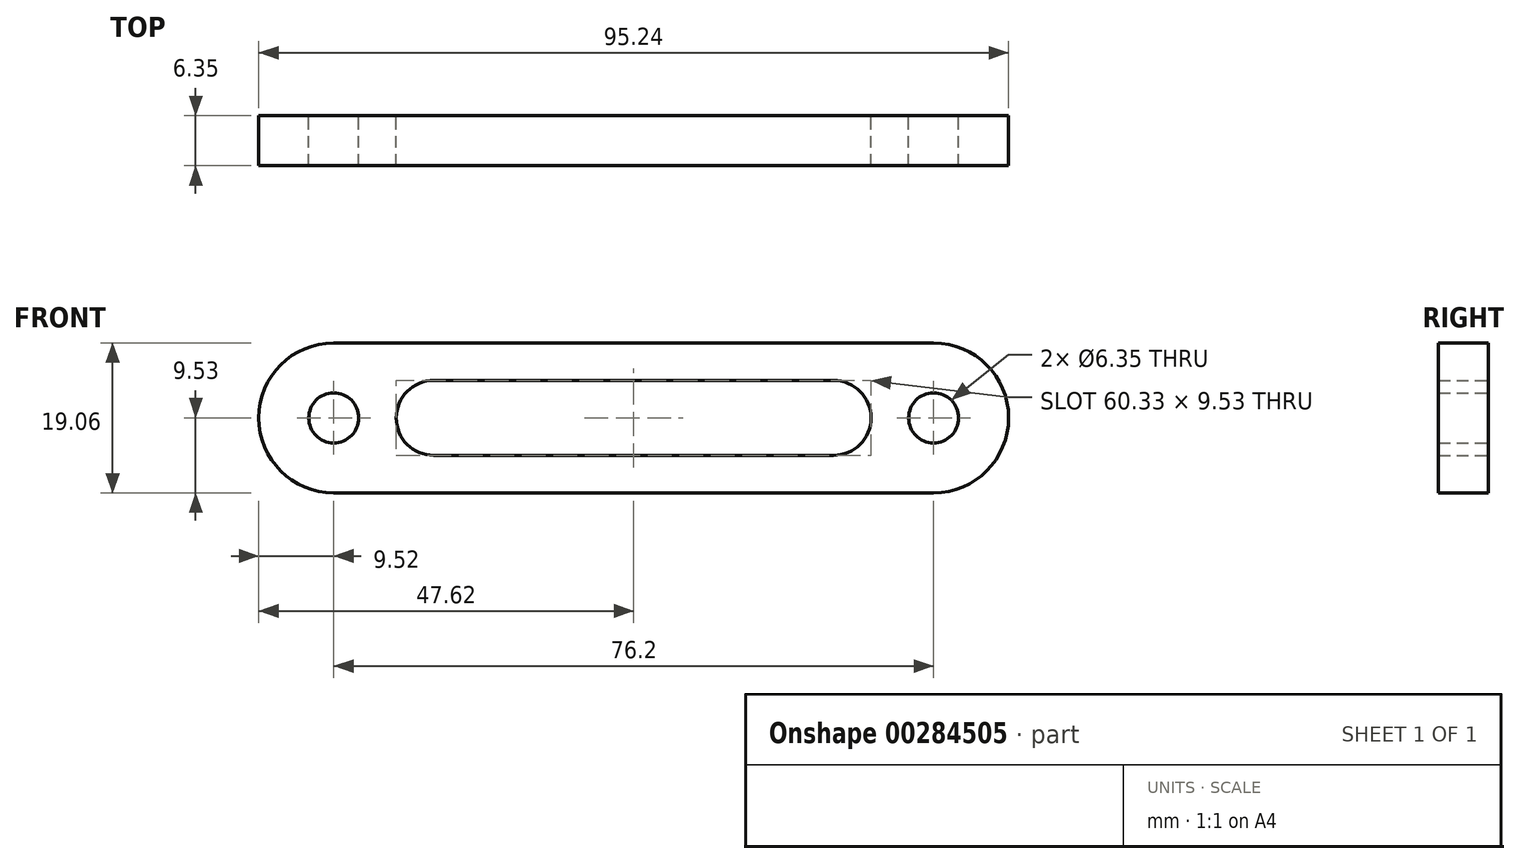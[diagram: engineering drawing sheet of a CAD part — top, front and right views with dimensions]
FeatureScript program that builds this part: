
annotation { "Feature Type Name" : "Feature", "Feature Type Description" : "" }
export const myFeature = defineFeature(function(context is Context, id is Id, definition is map)
    precondition{}
    {
        {
            var Q0;
            Q0=qCreatedBy(makeId("Front.planeOp"),FACE);
            var sketch = newSketch(context, id + "F0", { "sketchPlane" : qUnion([Q0])});
            skLineSegment(sketch, "E0.bottom", {"start": v(-38.1, 9.52) * mm, "end": v(38.1, 9.52) * mm});
            skLineSegment(sketch, "E0.top", {"start": v(-38.1, -9.52) * mm, "end": v(38.1, -9.52) * mm});
            skPoint(sketch, "E0.middle", {"position": v(0, 0) * mm});
            skArc(sketch, "E1", {"start": v(-38.1, 9.52) * mm, "mid": v(-47.62, 0) * mm, "end": v(-38.1, -9.52) * mm});
            skArc(sketch, "E2", {"start": v(38.1, -9.52) * mm, "mid": v(47.62, 0) * mm, "end": v(38.1, 9.52) * mm});
            skLineSegment(sketch, "E3.bottom", {"start": v(25.4, 4.76) * mm, "end": v(-25.4, 4.76) * mm});
            skLineSegment(sketch, "E3.top", {"start": v(25.4, -4.76) * mm, "end": v(-25.4, -4.76) * mm});
            skArc(sketch, "E4", {"start": v(-25.4, 4.76) * mm, "mid": v(-30.16, 0) * mm, "end": v(-25.4, -4.76) * mm});
            skArc(sketch, "E5", {"start": v(25.4, -4.76) * mm, "mid": v(30.16, 0) * mm, "end": v(25.4, 4.76) * mm});
            skCircle(sketch, "E6", {"center": v(-38.1, 0) * mm, "radius": 3.18 * mm});
            skCircle(sketch, "E7", {"center": v(38.1, 0) * mm, "radius": 3.18 * mm});
            skSolve(sketch);
        }
        {
            var Q0;
            Q0 = qSketchRegion(id + "F0", true);
            extrude(context, id + "F1", {"entities" : qUnion([Q0]), "depth" : 6.35 * mm});
        }
    });
